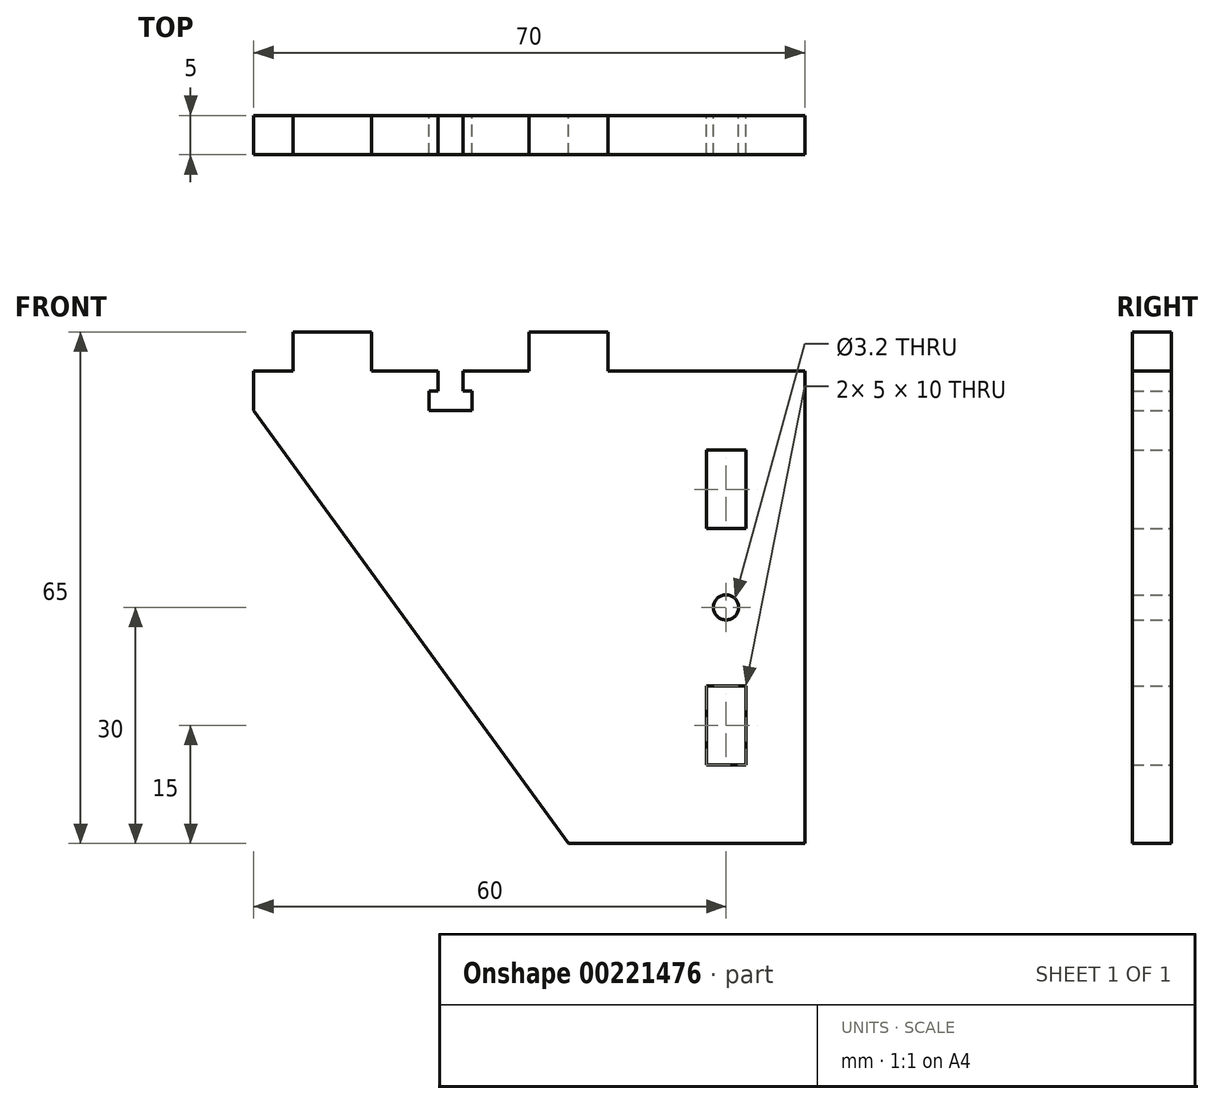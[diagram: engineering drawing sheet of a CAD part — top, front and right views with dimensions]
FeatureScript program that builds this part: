
annotation { "Feature Type Name" : "Feature", "Feature Type Description" : "" }
export const myFeature = defineFeature(function(context is Context, id is Id, definition is map)
    precondition{}
    {
        {
            assignVariable(context, id + "F0", {"name" : "thickness", "anyValue" : 5 * mm});
        }
        {
            var Q0;
            Q0=qCreatedBy(makeId("Front.planeOp"),FACE);
            var sketch = newSketch(context, id + "F1", { "sketchPlane" : qUnion([Q0])});
            skLineSegment(sketch, "E0", {"start": v(0, 0) * mm, "end": v(-30, 0) * mm});
            skLineSegment(sketch, "E1", {"start": v(-70, 60) * mm, "end": v(-65, 60) * mm});
            skLineSegment(sketch, "E2", {"start": v(0, 60) * mm, "end": v(0, 0) * mm});
            skLineSegment(sketch, "E3.bottom", {"start": v(-12.5, 10) * mm, "end": v(-7.5, 10) * mm});
            skLineSegment(sketch, "E3.top", {"start": v(-12.5, 20) * mm, "end": v(-7.5, 20) * mm});
            skLineSegment(sketch, "E3.left", {"start": v(-12.5, 10) * mm, "end": v(-12.5, 20) * mm});
            skLineSegment(sketch, "E3.right", {"start": v(-7.5, 10) * mm, "end": v(-7.5, 20) * mm});
            skLineSegment(sketch, "E4.bottom", {"start": v(-12.5, 40) * mm, "end": v(-7.5, 40) * mm});
            skLineSegment(sketch, "E4.top", {"start": v(-12.5, 50) * mm, "end": v(-7.5, 50) * mm});
            skLineSegment(sketch, "E4.left", {"start": v(-12.5, 40) * mm, "end": v(-12.5, 50) * mm});
            skLineSegment(sketch, "E4.right", {"start": v(-7.5, 40) * mm, "end": v(-7.5, 50) * mm});
            skCircle(sketch, "E5", {"center": v(-10, 30) * mm, "radius": 1.6 * mm});
            skPoint(sketch, "E5.centerSnap0", {"position": v(-10, 40) * mm});
            skPoint(sketch, "E5.centerSnap1", {"position": v(0, 30) * mm});
            skLineSegment(sketch, "E6", {"start": v(-65, 60) * mm, "end": v(-65, 65) * mm});
            skLineSegment(sketch, "E7", {"start": v(-65, 65) * mm, "end": v(-55, 65) * mm});
            skLineSegment(sketch, "E8", {"start": v(-55, 65) * mm, "end": v(-55, 60) * mm});
            skLineSegment(sketch, "E9", {"start": v(-35, 60) * mm, "end": v(-35, 65) * mm});
            skLineSegment(sketch, "E10", {"start": v(-35, 65) * mm, "end": v(-25, 65) * mm});
            skLineSegment(sketch, "E11", {"start": v(-25, 65) * mm, "end": v(-25, 60) * mm});
            skLineSegment(sketch, "E12", {"start": v(-46.6, 60) * mm, "end": v(-46.6, 57.5) * mm});
            skLineSegment(sketch, "E13", {"start": v(-46.6, 57.5) * mm, "end": v(-47.75, 57.5) * mm});
            skLineSegment(sketch, "E14", {"start": v(-47.75, 57.5) * mm, "end": v(-47.75, 55) * mm});
            skLineSegment(sketch, "E15", {"start": v(-47.75, 55) * mm, "end": v(-45, 55) * mm});
            skLineSegment(sketch, "E16", {"start": v(-45, 55) * mm, "end": v(-45, 60) * mm, "construction": true});
            skLineSegment(sketch, "E17.MirrorCS", {"start": v(-43.4, 57.5) * mm, "end": v(-42.25, 57.5) * mm});
            skLineSegment(sketch, "E18.MirrorCS", {"start": v(-42.25, 57.5) * mm, "end": v(-42.25, 55) * mm});
            skLineSegment(sketch, "E19.MirrorCS", {"start": v(-43.4, 60) * mm, "end": v(-43.4, 57.5) * mm});
            skLineSegment(sketch, "E20.MirrorCS", {"start": v(-42.25, 55) * mm, "end": v(-45, 55) * mm});
            skLineSegment(sketch, "E21.trimOffspring", {"start": v(-43.4, 60) * mm, "end": v(-35, 60) * mm});
            skLineSegment(sketch, "E22", {"start": v(-70, 60) * mm, "end": v(-70, 55) * mm});
            skLineSegment(sketch, "E23", {"start": v(-70, 55) * mm, "end": v(-30, 0) * mm});
            skLineSegment(sketch, "E24.trimOffspring", {"start": v(-25, 60) * mm, "end": v(0, 60) * mm});
            skLineSegment(sketch, "E25.trimOffspring", {"start": v(-55, 60) * mm, "end": v(-46.6, 60) * mm});
            skSolve(sketch);
        }
        {
            var Q0;
            Q0 = qSketchRegion(id + "F1", true);
            extrude(context, id + "F2", {"entities" : qUnion([Q0]), "depth" : getVariable(context, 'thickness')});
        }
    });
